# Revit family: Nemo_Sofa
name_source: partatom
category: Furniture
revit_build: Autodesk Revit Architecture 2014 (Build: 20131024_2115(x64)
units: mm (PartAtom-declared; Revit-internal decimal feet)

## types (1)
- Nemo_Sofa_
    Article Number = 158230
    BIMobject category = Furniture
    Depth = 910
    Depth Of Seat = 600 mm
    Description = The Nemo sofa is designed by Eero Koivisto and Ola Rune.
    Design country = Sweden
    Designer = Eero Koivisto/Ola Rune
    Edition number = 1
    Height = 655 mm  [stored 2.14895 ft]
    Height Of Seat = 390 mm  [stored 1.27953 ft]
    IFC Classification = Furniture
    Manufacturer = OFFECCT
    Manufacturer country = Sweden
    Manufacturer name = Offecct
    Manufacturer url = http://www.offecct.se
    Material Main = Fabric_Offecct_Nemo_Sofa_Blue
    Model = NEMO, Sofa
    Nominal height = 600
    Nominal width = 2270
    Product SKU = Nemo_Sofa_
    Product data url = http://www.offecct.se
    Product family = Furniture
    Product group = Chair
    QR Code = http://offecct.bimobject.com
    Technical description = http://www.offecct.se
    UNSPSC Code = 56
    UNSPSC Name = Furniture and Furnishings
    URL = http://www.offecct.se
    Weight Net (Kg) = 0
    Width = 2270 mm  [stored 7.44751 ft]

note: [stored X ft] marks values corroborated as IEEE doubles in the binary element streams (Revit-internal decimal feet)

## geometry (parser evidence)
native form markers: Blend x4, Sweep x1
no freeform markers — native parametric forms only
